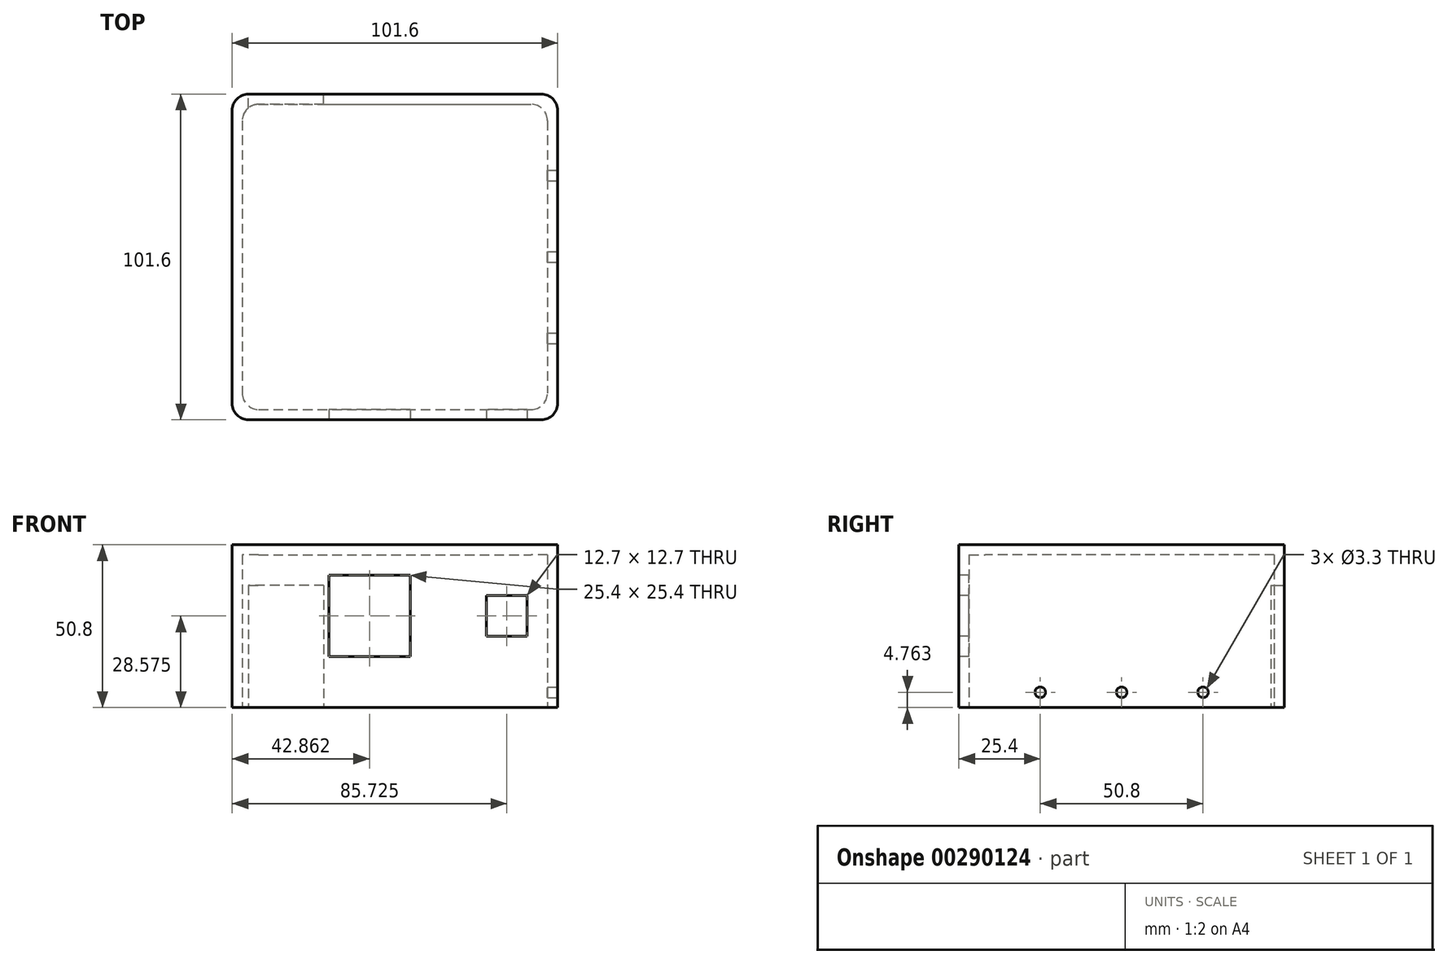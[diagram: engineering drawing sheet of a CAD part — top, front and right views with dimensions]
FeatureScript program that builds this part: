
annotation { "Feature Type Name" : "Feature", "Feature Type Description" : "" }
export const myFeature = defineFeature(function(context is Context, id is Id, definition is map)
    precondition{}
    {
        {
            var Q0;
            Q0=qCreatedBy(makeId("Top.planeOp"),FACE);
            var sketch = newSketch(context, id + "F0", { "sketchPlane" : qUnion([Q0])});
            skLineSegment(sketch, "E0.bottom", {"start": v(-50.8, 50.8) * mm, "end": v(50.8, 50.8) * mm});
            skLineSegment(sketch, "E0.top", {"start": v(-50.8, -50.8) * mm, "end": v(50.8, -50.8) * mm});
            skLineSegment(sketch, "E0.left", {"start": v(-50.8, 50.8) * mm, "end": v(-50.8, -50.8) * mm});
            skLineSegment(sketch, "E0.right", {"start": v(50.8, 50.8) * mm, "end": v(50.8, -50.8) * mm});
            skLineSegment(sketch, "E1.bottom", {"start": v(-47.63, 47.63) * mm, "end": v(47.63, 47.63) * mm});
            skLineSegment(sketch, "E1.top", {"start": v(-47.63, -47.63) * mm, "end": v(47.63, -47.63) * mm});
            skLineSegment(sketch, "E1.left", {"start": v(-47.63, 47.63) * mm, "end": v(-47.63, -47.63) * mm});
            skLineSegment(sketch, "E1.right", {"start": v(47.63, 47.63) * mm, "end": v(47.63, -47.63) * mm});
            skSolve(sketch);
        }
        {
            var Q0;
            Q0=makeQuery(id+"F0.imprint","IMPRINT",FACE,{"disambiguationData":[TD([[makeQuery(id+"F0.imprint","IMPRINT",EDGE,{"derivedFrom":sQuery(id+"F0.wireOp",EDGE,"E1.bottom")}),-1.0]])]});
            var Q1;
            Q1=makeQuery(id+"F0.imprint","IMPRINT",FACE,{"disambiguationData":[TD([[makeQuery(id+"F0.imprint","IMPRINT",EDGE,{"derivedFrom":sQuery(id+"F0.wireOp",EDGE,"E0.bottom")}),-1.0]])]});
            extrude(context, id + "F1", {"entities" : qUnion([Q0, Q1]), "depth" : 50.8 * mm});
        }
        {
            var Q0;
            Q0=makeQuery(id+"F0.imprint","IMPRINT",FACE,{"disambiguationData":[TD([[makeQuery(id+"F0.imprint","IMPRINT",EDGE,{"derivedFrom":sQuery(id+"F0.wireOp",EDGE,"E1.bottom")}),-1.0]])]});
            extrude(context, id + "F2", {"entities" : qUnion([Q0]), "operationType" : NewBodyOperationType.REMOVE, "depth" : 47.62 * mm});
        }
        {
            var Q0;
            Q0=makeQuery(id+"F1.opExtrude","SWEPT_EDGE",EDGE,{"disambiguationData":[OSD([sQuery(id+"F0.wireOp",EDGE,"E0.top"),sQuery(id+"F0.wireOp",EDGE,"E0.right")])]});
            var Q1;
            Q1=makeQuery(id+"F1.opExtrude","SWEPT_EDGE",EDGE,{"disambiguationData":[OSD([sQuery(id+"F0.wireOp",EDGE,"E0.bottom"),sQuery(id+"F0.wireOp",EDGE,"E0.right")])]});
            var Q2;
            Q2=makeQuery(id+"F1.opExtrude","SWEPT_EDGE",EDGE,{"disambiguationData":[OSD([sQuery(id+"F0.wireOp",EDGE,"E0.bottom"),sQuery(id+"F0.wireOp",EDGE,"E0.left")])]});
            var Q3;
            Q3=makeQuery(id+"F2.boolean.opBoolean","COPY",EDGE,{"derivedFrom":makeQuery(id+"F2.opExtrude","SWEPT_EDGE",EDGE,{"disambiguationData":[OSD([sQuery(id+"F0.wireOp",EDGE,"E1.top"),sQuery(id+"F0.wireOp",EDGE,"E1.left")])]})});
            var Q4;
            Q4=makeQuery(id+"F2.boolean.opBoolean","COPY",EDGE,{"derivedFrom":makeQuery(id+"F2.opExtrude","SWEPT_EDGE",EDGE,{"disambiguationData":[OSD([sQuery(id+"F0.wireOp",EDGE,"E1.top"),sQuery(id+"F0.wireOp",EDGE,"E1.right")])]})});
            var Q5;
            Q5=makeQuery(id+"F2.boolean.opBoolean","COPY",EDGE,{"derivedFrom":makeQuery(id+"F2.opExtrude","SWEPT_EDGE",EDGE,{"disambiguationData":[OSD([sQuery(id+"F0.wireOp",EDGE,"E1.bottom"),sQuery(id+"F0.wireOp",EDGE,"E1.right")])]})});
            var Q6;
            Q6=makeQuery(id+"F2.boolean.opBoolean","COPY",EDGE,{"derivedFrom":makeQuery(id+"F2.opExtrude","SWEPT_EDGE",EDGE,{"disambiguationData":[OSD([sQuery(id+"F0.wireOp",EDGE,"E1.bottom"),sQuery(id+"F0.wireOp",EDGE,"E1.left")])]})});
            var Q7;
            Q7=makeQuery(id+"F1.opExtrude","SWEPT_EDGE",EDGE,{"disambiguationData":[OSD([sQuery(id+"F0.wireOp",EDGE,"E0.top"),sQuery(id+"F0.wireOp",EDGE,"E0.left")])]});
            fillet(context, id + "F3", {"entities" : qUnion([Q0, Q1, Q2, Q3, Q4, Q5, Q6, Q7]), "radius" : 5.08 * mm, "tangentPropagation" : true, "allowEdgeOverflow" : false});
        }
        {
            var Q0;
            Q0=makeQuery(id+"F1.opExtrude","SWEPT_FACE",FACE,{"disambiguationData":[OSD([sQuery(id+"F0.wireOp",EDGE,"E0.top")])]});
            var sketch = newSketch(context, id + "F4", { "sketchPlane" : qUnion([Q0])});
            skLineSegment(sketch, "E2.bottom", {"start": v(28.58, 34.93) * mm, "end": v(41.28, 34.93) * mm});
            skLineSegment(sketch, "E2.top", {"start": v(28.58, 22.23) * mm, "end": v(41.28, 22.23) * mm});
            skLineSegment(sketch, "E2.left", {"start": v(28.58, 34.93) * mm, "end": v(28.58, 22.23) * mm});
            skLineSegment(sketch, "E2.right", {"start": v(41.28, 34.93) * mm, "end": v(41.28, 22.23) * mm});
            skLineSegment(sketch, "E3.bottom", {"start": v(-20.64, 41.28) * mm, "end": v(4.76, 41.28) * mm});
            skLineSegment(sketch, "E3.top", {"start": v(-20.64, 15.88) * mm, "end": v(4.76, 15.88) * mm});
            skLineSegment(sketch, "E3.left", {"start": v(-20.64, 41.28) * mm, "end": v(-20.64, 15.88) * mm});
            skLineSegment(sketch, "E3.right", {"start": v(4.76, 41.28) * mm, "end": v(4.76, 15.88) * mm});
            skSolve(sketch);
        }
        {
            var Q0;
            Q0=makeQuery(id+"F4.imprint","IMPRINT",FACE,{"disambiguationData":[TD([[makeQuery(id+"F4.imprint","IMPRINT",EDGE,{"derivedFrom":sQuery(id+"F4.wireOp",EDGE,"E3.bottom")}),-1.0]])]});
            var Q1;
            Q1=makeQuery(id+"F4.imprint","IMPRINT",FACE,{"disambiguationData":[TD([[makeQuery(id+"F4.imprint","IMPRINT",EDGE,{"derivedFrom":sQuery(id+"F4.wireOp",EDGE,"E2.bottom")}),-1.0]])]});
            extrude(context, id + "F5", {"entities" : qUnion([Q0, Q1]), "operationType" : NewBodyOperationType.REMOVE, "oppositeDirection" : true, "depth" : 5.08 * mm});
        }
        {
            var Q0;
            Q0=makeQuery(id+"F1.opExtrude","SWEPT_FACE",FACE,{"disambiguationData":[OSD([sQuery(id+"F0.wireOp",EDGE,"E0.bottom")])]});
            var sketch = newSketch(context, id + "F6", { "sketchPlane" : qUnion([Q0])});
            skLineSegment(sketch, "E4.bottom", {"start": v(22.23, 38.1) * mm, "end": v(47.62, 38.1) * mm});
            skLineSegment(sketch, "E4.top", {"start": v(22.23, 0) * mm, "end": v(47.62, 0) * mm});
            skLineSegment(sketch, "E4.left", {"start": v(22.23, 38.1) * mm, "end": v(22.23, 0) * mm});
            skLineSegment(sketch, "E4.right", {"start": v(47.62, 38.1) * mm, "end": v(47.62, 0) * mm});
            skSolve(sketch);
        }
        {
            var Q0;
            {var subQ0=sQuery(id+"F6.wireOp",EDGE,"E4.left");Q0=makeQuery(id+"F6.imprint","IMPRINT",FACE,{"disambiguationData":[TD([[makeQuery(id+"F6.imprint","IMPRINT",EDGE,{"derivedFrom":subQ0}),1.0]])]});}
            extrude(context, id + "F7", {"entities" : qUnion([Q0]), "operationType" : NewBodyOperationType.REMOVE, "oppositeDirection" : true, "depth" : 25.4 * mm});
        }
        {
            var Q0;
            Q0=makeQuery(id+"F1.opExtrude","SWEPT_FACE",FACE,{"disambiguationData":[OSD([sQuery(id+"F0.wireOp",EDGE,"E0.right")])]});
            var sketch = newSketch(context, id + "F8", { "sketchPlane" : qUnion([Q0])});
            skPoint(sketch, "E5", {"position": v(-25.4, 4.76) * mm});
            skPoint(sketch, "E6.1.0.0", {"position": v(0, 4.76) * mm});
            skPoint(sketch, "E6.2.0.0", {"position": v(25.4, 4.76) * mm});
            skLineSegment(sketch, "E6.direction1", {"start": v(-25.4, 4.76) * mm, "end": v(0, 4.76) * mm, "construction": true});
            skSolve(sketch);
        }
        {
            var Q0;
            Q0=sQuery(id+"F8.wireOp",VERTEX,"E5");
            var Q1;
            Q1=sQuery(id+"F8.wireOp",VERTEX,"E6.1.0.0");
            var Q2;
            Q2=sQuery(id+"F8.wireOp",VERTEX,"E6.2.0.0");
            var Q3;
            Q3=makeQuery(id+"F1.opExtrude","SWEPT_BODY",BODY,{"disambiguationData":[OSD([sQuery(id+"F0.wireOp",EDGE,"E0.bottom"),sQuery(id+"F0.wireOp",EDGE,"E0.top"),sQuery(id+"F0.wireOp",EDGE,"E0.left"),sQuery(id+"F0.wireOp",EDGE,"E0.right")])]});
            hole(context, id + "F9", {"style" : HoleStyle.SIMPLE, "endStyle" : HoleEndStyle.BLIND, "standardTappedOrClearance" : lookupTablePath({ "standard" : "ISO", "fit" : "Normal", "size" : "M3", "type" : "Clearance" }), "standardBlindInLast" : lookupTablePath({ "fit" : "Standard", "standard" : "ISO", "size" : "M3", "type" : "Clearance" }), "holeDiameter" : 3.3 * mm, "holeDepth" : 6.35 * mm, "tappedDepth" : 12.7 * mm, "tapClearance" : 3, "startFromSketch" : true, "locations" : qUnion([Q0, Q1, Q2]), "scope" : qUnion([Q3])});
        }
    });
